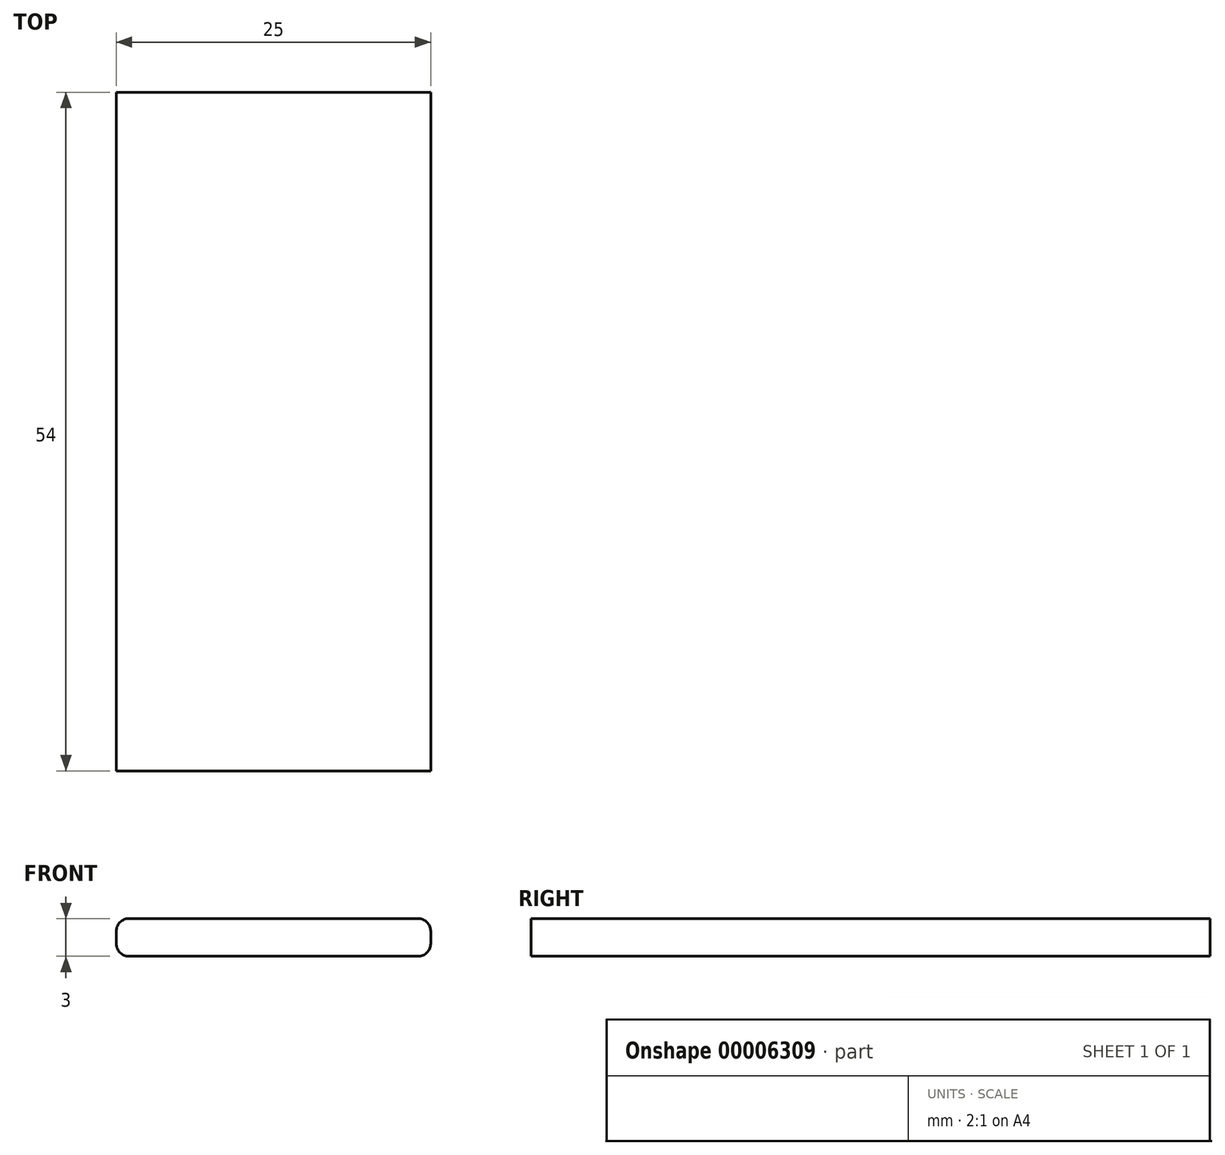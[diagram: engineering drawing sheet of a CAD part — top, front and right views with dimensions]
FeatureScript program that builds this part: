
annotation { "Feature Type Name" : "Feature", "Feature Type Description" : "" }
export const myFeature = defineFeature(function(context is Context, id is Id, definition is map)
    precondition{}
    {
        {
            var Q0;
            Q0=qCreatedBy(makeId("Front.planeOp"),FACE);
            var sketch = newSketch(context, id + "F0", { "sketchPlane" : qUnion([Q0])});
            skLineSegment(sketch, "E0.bottom", {"start": v(1, 0) * mm, "end": v(24, 0) * mm});
            skLineSegment(sketch, "E0.top", {"start": v(1, 3) * mm, "end": v(24, 3) * mm});
            skLineSegment(sketch, "E0.left", {"start": v(0, 1) * mm, "end": v(0, 2) * mm});
            skLineSegment(sketch, "E0.right", {"start": v(25, 1) * mm, "end": v(25, 2) * mm});
            skPoint(sketch, "E1.visualSharp", {"position": v(0, 3) * mm});
            skArc(sketch, "E1.filletArc", {"start": v(1, 3) * mm, "mid": v(0.3, 2.7) * mm, "end": v(0, 2) * mm});
            skPoint(sketch, "E2.visualSharp", {"position": v(0, 0) * mm});
            skArc(sketch, "E2.filletArc", {"start": v(0, 1) * mm, "mid": v(0.3, 0.3) * mm, "end": v(1, 0) * mm});
            skPoint(sketch, "E3.visualSharp", {"position": v(25, 3) * mm});
            skArc(sketch, "E3.filletArc", {"start": v(25, 2) * mm, "mid": v(24.7, 2.7) * mm, "end": v(24, 3) * mm});
            skPoint(sketch, "E4.visualSharp", {"position": v(25, 0) * mm});
            skArc(sketch, "E4.filletArc", {"start": v(24, 0) * mm, "mid": v(24.7, 0.3) * mm, "end": v(25, 1) * mm});
            skSolve(sketch);
        }
        {
            var Q0;
            Q0=makeQuery(id+"F0.imprint","IMPRINT",FACE,{"disambiguationData":[TD([[makeQuery(id+"F0.imprint","IMPRINT",EDGE,{"derivedFrom":sQuery(id+"F0.wireOp",EDGE,"E0.bottom")}),1.0]])]});
            extrude(context, id + "F1", {"entities" : qUnion([Q0]), "endBound" : BoundingType.SYMMETRIC, "depth" : 54 * mm});
        }
        {
            var Q0;
            Q0=makeQuery(id+"F1.opExtrude","SWEPT_BODY",BODY,{"disambiguationData":[OSD([sQuery(id+"F0.wireOp",EDGE,"E0.bottom"),sQuery(id+"F0.wireOp",EDGE,"E0.top"),sQuery(id+"F0.wireOp",EDGE,"E0.left"),sQuery(id+"F0.wireOp",EDGE,"E0.right"),sQuery(id+"F0.wireOp",EDGE,"E1.filletArc"),sQuery(id+"F0.wireOp",EDGE,"E2.filletArc"),sQuery(id+"F0.wireOp",EDGE,"E3.filletArc"),sQuery(id+"F0.wireOp",EDGE,"E4.filletArc")])]});
            transform(context, id + "F2", {"entities" : qUnion([Q0]), "transformType" : TransformType.TRANSLATION_3D, "dx" : 0 * mm, "dy" : 0 * mm, "dz" : 0 * mm, "makeCopy" : true});
        }
    });
